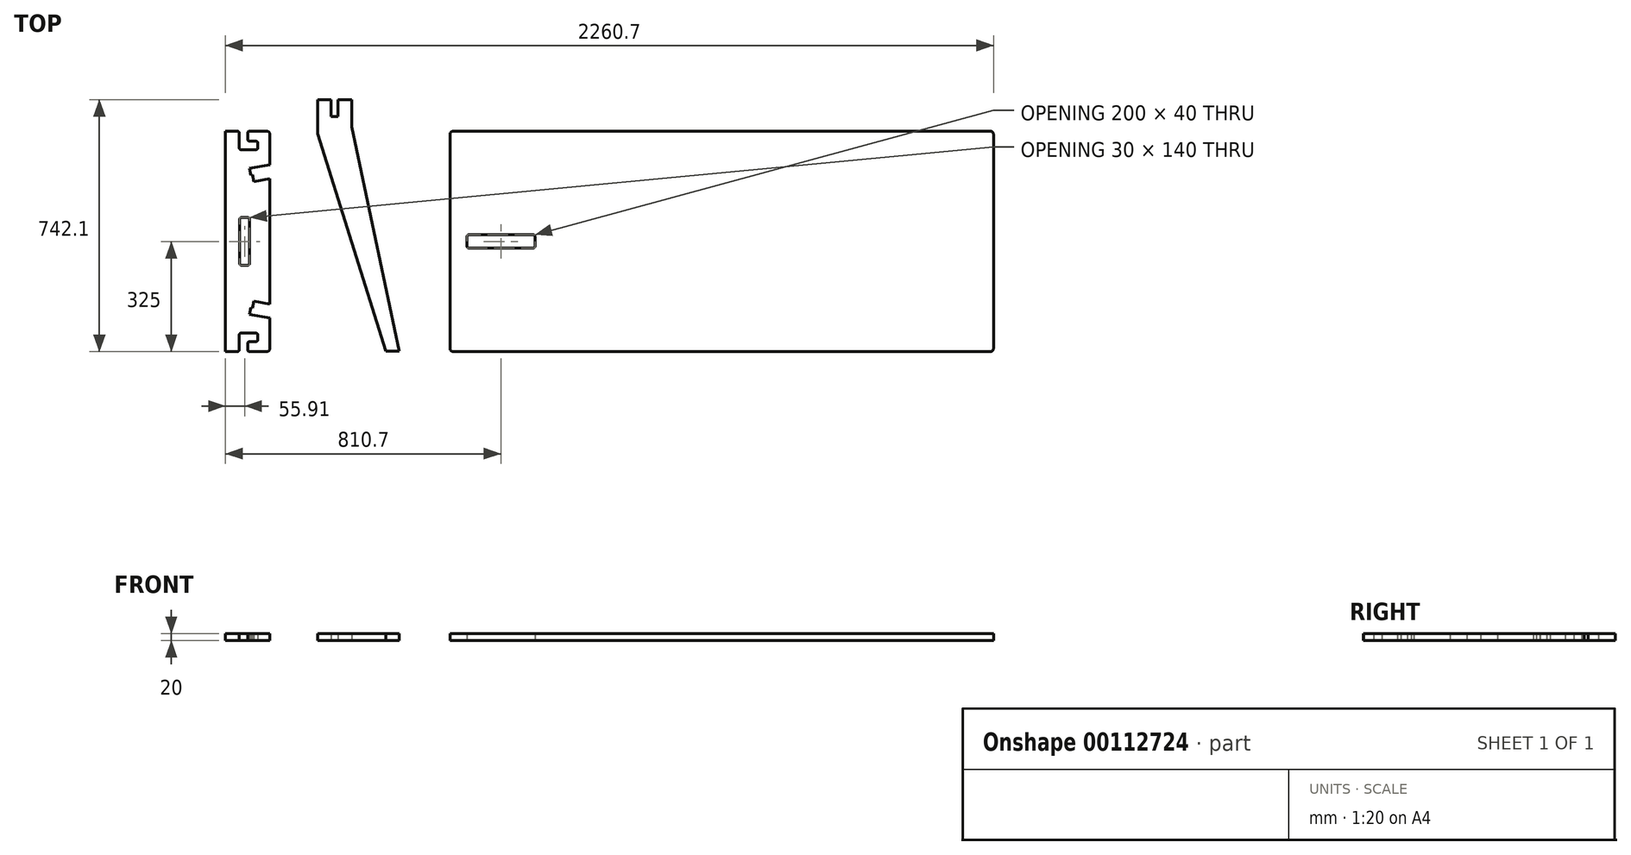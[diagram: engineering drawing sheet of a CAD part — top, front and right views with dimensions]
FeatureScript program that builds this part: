
annotation { "Feature Type Name" : "Feature", "Feature Type Description" : "" }
export const myFeature = defineFeature(function(context is Context, id is Id, definition is map)
    precondition{}
    {
        {
            assignVariable(context, id + "F0", {"name" : "stock_thickness", "anyValue" : 20});
        }
        {
            var Q0;
            Q0=qCreatedBy(makeId("Top.planeOp"),FACE);
            var sketch = newSketch(context, id + "F1", { "sketchPlane" : qUnion([Q0])});
            skLineSegment(sketch, "E0.bottom", {"start": v(10, 0) * mm, "end": v(1590, 0) * mm});
            skLineSegment(sketch, "E0.top", {"start": v(10, 650) * mm, "end": v(1590, 650) * mm});
            skLineSegment(sketch, "E0.left", {"start": v(0, 10) * mm, "end": v(0, 640) * mm});
            skLineSegment(sketch, "E0.right", {"start": v(1600, 10) * mm, "end": v(1600, 640) * mm});
            skPoint(sketch, "E1.visualSharp", {"position": v(0, 650) * mm});
            skArc(sketch, "E1.filletArc", {"start": v(10, 650) * mm, "mid": v(2.93, 647.07) * mm, "end": v(0, 640) * mm});
            skPoint(sketch, "E2.visualSharp", {"position": v(1600, 650) * mm});
            skArc(sketch, "E2.filletArc", {"start": v(1600, 640) * mm, "mid": v(1597.07, 647.07) * mm, "end": v(1590, 650) * mm});
            skPoint(sketch, "E3.visualSharp", {"position": v(1600, 0) * mm});
            skArc(sketch, "E3.filletArc", {"start": v(1590, 0) * mm, "mid": v(1597.07, 2.93) * mm, "end": v(1600, 10) * mm});
            skPoint(sketch, "E4.visualSharp", {"position": v(0, 0) * mm});
            skArc(sketch, "E4.filletArc", {"start": v(0, 10) * mm, "mid": v(2.93, 2.93) * mm, "end": v(10, 0) * mm});
            skLineSegment(sketch, "E5", {"start": v(0, 325) * mm, "end": v(1600, 325) * mm, "construction": true});
            skLineSegment(sketch, "E6", {"start": v(800, 650) * mm, "end": v(800, 0) * mm, "construction": true});
            skCircle(sketch, "E7", {"center": v(800, 325) * mm, "radius": 30 * mm, "construction": true});
            skLineSegment(sketch, "E8.bottom", {"start": v(1544, 305) * mm, "end": v(1356, 305) * mm});
            skLineSegment(sketch, "E8.top", {"start": v(1544, 345) * mm, "end": v(1356, 345) * mm});
            skLineSegment(sketch, "E8.left", {"start": v(1550, 311) * mm, "end": v(1550, 339) * mm});
            skLineSegment(sketch, "E8.right", {"start": v(1350, 311) * mm, "end": v(1350, 339) * mm});
            skPoint(sketch, "E8.middle", {"position": v(1450, 325) * mm});
            skLineSegment(sketch, "E9.bottom", {"start": v(1544, 355) * mm, "end": v(1356, 355) * mm});
            skLineSegment(sketch, "E9.top", {"start": v(1544, 369) * mm, "end": v(1356, 369) * mm});
            skLineSegment(sketch, "E9.left", {"start": v(1550, 361) * mm, "end": v(1550, 363) * mm});
            skLineSegment(sketch, "E9.right", {"start": v(1350, 361) * mm, "end": v(1350, 363) * mm});
            skPoint(sketch, "E9.middle", {"position": v(1450, 362) * mm});
            skCircle(sketch, "E10.1.0.0", {"center": v(885, 325) * mm, "radius": 30 * mm, "construction": true});
            skCircle(sketch, "E10.2.0.0", {"center": v(970, 325) * mm, "radius": 30 * mm, "construction": true});
            skLineSegment(sketch, "E10.direction1", {"start": v(800, 325) * mm, "end": v(885, 325) * mm, "construction": true});
            skCircle(sketch, "E11.0.3.0", {"center": v(1055, 325) * mm, "radius": 30 * mm, "construction": true});
            skPoint(sketch, "E12.visualSharp", {"position": v(1350, 345) * mm});
            skArc(sketch, "E12.filletArc", {"start": v(1356, 345) * mm, "mid": v(1351.76, 343.24) * mm, "end": v(1350, 339) * mm});
            skPoint(sketch, "E13.visualSharp", {"position": v(1550, 345) * mm});
            skArc(sketch, "E13.filletArc", {"start": v(1550, 339) * mm, "mid": v(1548.24, 343.24) * mm, "end": v(1544, 345) * mm});
            skPoint(sketch, "E14.visualSharp", {"position": v(1550, 305) * mm});
            skArc(sketch, "E14.filletArc", {"start": v(1544, 305) * mm, "mid": v(1548.24, 306.76) * mm, "end": v(1550, 311) * mm});
            skPoint(sketch, "E15.visualSharp", {"position": v(1350, 305) * mm});
            skArc(sketch, "E15.filletArc", {"start": v(1350, 311) * mm, "mid": v(1351.76, 306.76) * mm, "end": v(1356, 305) * mm});
            skPoint(sketch, "E16.visualSharp", {"position": v(1350, 369) * mm});
            skArc(sketch, "E16.filletArc", {"start": v(1356, 369) * mm, "mid": v(1351.76, 367.24) * mm, "end": v(1350, 363) * mm});
            skPoint(sketch, "E17.visualSharp", {"position": v(1350, 355) * mm});
            skArc(sketch, "E17.filletArc", {"start": v(1350, 361) * mm, "mid": v(1351.76, 356.76) * mm, "end": v(1356, 355) * mm});
            skPoint(sketch, "E18.visualSharp", {"position": v(1550, 355) * mm});
            skArc(sketch, "E18.filletArc", {"start": v(1544, 355) * mm, "mid": v(1548.24, 356.76) * mm, "end": v(1550, 361) * mm});
            skPoint(sketch, "E19.visualSharp", {"position": v(1550, 369) * mm});
            skArc(sketch, "E19.filletArc", {"start": v(1550, 363) * mm, "mid": v(1548.24, 367.24) * mm, "end": v(1544, 369) * mm});
            skArc(sketch, "E20.MirrorCS", {"start": v(250, 361) * mm, "mid": v(248.24, 356.76) * mm, "end": v(244, 355) * mm});
            skArc(sketch, "E21.MirrorCS", {"start": v(244, 369) * mm, "mid": v(248.24, 367.24) * mm, "end": v(250, 363) * mm});
            skArc(sketch, "E22.MirrorCS", {"start": v(50, 363) * mm, "mid": v(51.76, 367.24) * mm, "end": v(56, 369) * mm});
            skArc(sketch, "E23.MirrorCS", {"start": v(56, 355) * mm, "mid": v(51.76, 356.76) * mm, "end": v(50, 361) * mm});
            skArc(sketch, "E24.MirrorCS", {"start": v(50, 339) * mm, "mid": v(51.76, 343.24) * mm, "end": v(56, 345) * mm});
            skArc(sketch, "E25.MirrorCS", {"start": v(250, 311) * mm, "mid": v(248.24, 306.76) * mm, "end": v(244, 305) * mm});
            skArc(sketch, "E26.MirrorCS", {"start": v(244, 345) * mm, "mid": v(248.24, 343.24) * mm, "end": v(250, 339) * mm});
            skArc(sketch, "E27.MirrorCS", {"start": v(56, 305) * mm, "mid": v(51.76, 306.76) * mm, "end": v(50, 311) * mm});
            skPoint(sketch, "E28.MirrorP", {"position": v(250, 355) * mm});
            skPoint(sketch, "E29.MirrorP", {"position": v(50, 355) * mm});
            skCircle(sketch, "E30.MirrorC", {"center": v(630, 325) * mm, "radius": 30 * mm, "construction": true});
            skPoint(sketch, "E31.MirrorP", {"position": v(50, 369) * mm});
            skLineSegment(sketch, "E32.MirrorCS", {"start": v(50, 311) * mm, "end": v(50, 339) * mm});
            skLineSegment(sketch, "E33.MirrorCS", {"start": v(250, 311) * mm, "end": v(250, 339) * mm});
            skLineSegment(sketch, "E34.MirrorCS", {"start": v(56, 355) * mm, "end": v(244, 355) * mm});
            skPoint(sketch, "E35.MirrorP", {"position": v(50, 305) * mm});
            skCircle(sketch, "E36.MirrorC", {"center": v(715, 325) * mm, "radius": 30 * mm, "construction": true});
            skPoint(sketch, "E37.MirrorP", {"position": v(150, 362) * mm});
            skLineSegment(sketch, "E38.MirrorCS", {"start": v(56, 369) * mm, "end": v(244, 369) * mm});
            skPoint(sketch, "E39.MirrorP", {"position": v(50, 345) * mm});
            skPoint(sketch, "E40.MirrorP", {"position": v(150, 325) * mm});
            skCircle(sketch, "E41.MirrorC", {"center": v(545, 325) * mm, "radius": 30 * mm, "construction": true});
            skPoint(sketch, "E42.MirrorP", {"position": v(250, 369) * mm});
            skLineSegment(sketch, "E43.MirrorCS", {"start": v(56, 305) * mm, "end": v(244, 305) * mm});
            skLineSegment(sketch, "E44.MirrorCS", {"start": v(56, 345) * mm, "end": v(244, 345) * mm});
            skPoint(sketch, "E45.MirrorP", {"position": v(250, 345) * mm});
            skPoint(sketch, "E46.MirrorP", {"position": v(250, 305) * mm});
            skArc(sketch, "E47.MirrorCS", {"start": v(50, 287) * mm, "mid": v(51.76, 282.76) * mm, "end": v(56, 281) * mm});
            skArc(sketch, "E48.MirrorCS", {"start": v(244, 281) * mm, "mid": v(248.24, 282.76) * mm, "end": v(250, 287) * mm});
            skLineSegment(sketch, "E49.MirrorCS", {"start": v(56, 295) * mm, "end": v(244, 295) * mm});
            skPoint(sketch, "E50.MirrorP", {"position": v(250, 281) * mm});
            skLineSegment(sketch, "E51.MirrorCS", {"start": v(56, 281) * mm, "end": v(244, 281) * mm});
            skArc(sketch, "E52.MirrorCS", {"start": v(56, 295) * mm, "mid": v(51.76, 293.24) * mm, "end": v(50, 289) * mm});
            skArc(sketch, "E53.MirrorCS", {"start": v(250, 289) * mm, "mid": v(248.24, 293.24) * mm, "end": v(244, 295) * mm});
            skPoint(sketch, "E54.MirrorP", {"position": v(150, 288) * mm});
            skPoint(sketch, "E55.MirrorP", {"position": v(50, 281) * mm});
            skArc(sketch, "E56.MirrorCS", {"start": v(1350, 289) * mm, "mid": v(1351.76, 293.24) * mm, "end": v(1356, 295) * mm});
            skArc(sketch, "E57.MirrorCS", {"start": v(1550, 287) * mm, "mid": v(1548.24, 282.76) * mm, "end": v(1544, 281) * mm});
            skArc(sketch, "E58.MirrorCS", {"start": v(1544, 295) * mm, "mid": v(1548.24, 293.24) * mm, "end": v(1550, 289) * mm});
            skArc(sketch, "E59.MirrorCS", {"start": v(1356, 281) * mm, "mid": v(1351.76, 282.76) * mm, "end": v(1350, 287) * mm});
            skPoint(sketch, "E60.MirrorP", {"position": v(1350, 295) * mm});
            skPoint(sketch, "E61.MirrorP", {"position": v(1550, 295) * mm});
            skPoint(sketch, "E62.MirrorP", {"position": v(1450, 288) * mm});
            skPoint(sketch, "E63.MirrorP", {"position": v(1350, 281) * mm});
            skLineSegment(sketch, "E64.MirrorCS", {"start": v(1544, 295) * mm, "end": v(1356, 295) * mm});
            skLineSegment(sketch, "E65.MirrorCS", {"start": v(1544, 281) * mm, "end": v(1356, 281) * mm});
            skPoint(sketch, "E66.MirrorP", {"position": v(1550, 281) * mm});
            skSolve(sketch);
        }
        {
            var Q0;
            Q0=qCreatedBy(makeId("Top.planeOp"),FACE);
            var sketch = newSketch(context, id + "F2", { "sketchPlane" : qUnion([Q0])});
            skLineSegment(sketch, "E67.bottom", {"start": v(-148.98, 2.1) * mm, "end": v(-188.98, 2.1) * mm});
            skLineSegment(sketch, "E67.top", {"start": v(-288.98, 742.1) * mm, "end": v(-329.98, 742.1) * mm});
            skLineSegment(sketch, "E68", {"start": v(-288.98, 742.1) * mm, "end": v(-288.98, 662.1) * mm});
            skLineSegment(sketch, "E69", {"start": v(-288.98, 662.1) * mm, "end": v(-148.98, 2.1) * mm});
            skLineSegment(sketch, "E70", {"start": v(-388.98, 642.1) * mm, "end": v(-188.98, 2.1) * mm});
            skLineSegment(sketch, "E71", {"start": v(-388.98, 742.1) * mm, "end": v(-388.98, 2.1) * mm, "construction": true});
            skLineSegment(sketch, "E72", {"start": v(-388.98, 742.1) * mm, "end": v(-388.98, 642.1) * mm});
            skLineSegment(sketch, "E73.bottom", {"start": v(-329.98, 692.1) * mm, "end": v(-349.98, 692.1) * mm});
            skLineSegment(sketch, "E73.left", {"start": v(-329.98, 692.1) * mm, "end": v(-329.98, 742.1) * mm});
            skLineSegment(sketch, "E73.right", {"start": v(-349.98, 692.1) * mm, "end": v(-349.98, 742.1) * mm});
            skPoint(sketch, "E73.middle", {"position": v(-338.98, 742.1) * mm});
            skLineSegment(sketch, "E74.trimOffspring", {"start": v(-349.98, 742.1) * mm, "end": v(-388.98, 742.1) * mm});
            skSolve(sketch);
        }
        {
            var Q0;
            Q0=qCreatedBy(makeId("Top.planeOp"),FACE);
            var sketch = newSketch(context, id + "F3", { "sketchPlane" : qUnion([Q0])});
            skLineSegment(sketch, "E75.bottom", {"start": v(-540.7, 0) * mm, "end": v(-589.7, 0) * mm});
            skLineSegment(sketch, "E75.top", {"start": v(-540.7, 650) * mm, "end": v(-589.7, 650) * mm});
            skLineSegment(sketch, "E75.left", {"start": v(-530.7, 10) * mm, "end": v(-530.7, 640) * mm});
            skLineSegment(sketch, "E75.right", {"start": v(-660.7, 0) * mm, "end": v(-660.7, 650) * mm});
            skLineSegment(sketch, "E76", {"start": v(-530.7, 325) * mm, "end": v(-589.8, 325) * mm, "construction": true});
            skLineSegment(sketch, "E77", {"start": v(-530.7, 100) * mm, "end": v(-589.8, 110.32) * mm});
            skLineSegment(sketch, "E78", {"start": v(-589.8, 110.32) * mm, "end": v(-586.37, 130.02) * mm});
            skLineSegment(sketch, "E79", {"start": v(-586.37, 130.02) * mm, "end": v(-581.44, 129.16) * mm});
            skLineSegment(sketch, "E80", {"start": v(-581.44, 129.16) * mm, "end": v(-578, 148.86) * mm});
            skLineSegment(sketch, "E81", {"start": v(-578, 148.86) * mm, "end": v(-530.7, 140.6) * mm});
            skLineSegment(sketch, "E82", {"start": v(-595.7, 6) * mm, "end": v(-595.7, 24) * mm});
            skLineSegment(sketch, "E83", {"start": v(-589.7, 30) * mm, "end": v(-571.7, 30) * mm});
            skLineSegment(sketch, "E84", {"start": v(-620.7, 6) * mm, "end": v(-620.7, 49) * mm});
            skLineSegment(sketch, "E85", {"start": v(-614.7, 55) * mm, "end": v(-571.7, 55) * mm});
            skLineSegment(sketch, "E86", {"start": v(-565.7, 49) * mm, "end": v(-565.7, 36) * mm});
            skLineSegment(sketch, "E87.trimOffspring", {"start": v(-626.7, 0) * mm, "end": v(-660.7, 0) * mm});
            skPoint(sketch, "E88.visualSharp", {"position": v(-595.7, 30) * mm});
            skArc(sketch, "E88.filletArc", {"start": v(-589.7, 30) * mm, "mid": v(-593.94, 28.24) * mm, "end": v(-595.7, 24) * mm});
            skPoint(sketch, "E89.visualSharp", {"position": v(-620.7, 0) * mm});
            skArc(sketch, "E89.filletArc", {"start": v(-626.7, 0) * mm, "mid": v(-622.46, 1.76) * mm, "end": v(-620.7, 6) * mm});
            skPoint(sketch, "E90.visualSharp", {"position": v(-595.7, 0) * mm});
            skArc(sketch, "E90.filletArc", {"start": v(-595.7, 6) * mm, "mid": v(-593.94, 1.76) * mm, "end": v(-589.7, 0) * mm});
            skPoint(sketch, "E91.visualSharp", {"position": v(-565.7, 30) * mm});
            skArc(sketch, "E91.filletArc", {"start": v(-571.7, 30) * mm, "mid": v(-567.46, 31.76) * mm, "end": v(-565.7, 36) * mm});
            skPoint(sketch, "E92.visualSharp", {"position": v(-565.7, 55) * mm});
            skArc(sketch, "E92.filletArc", {"start": v(-565.7, 49) * mm, "mid": v(-567.46, 53.24) * mm, "end": v(-571.7, 55) * mm});
            skPoint(sketch, "E93.visualSharp", {"position": v(-620.7, 55) * mm});
            skArc(sketch, "E93.filletArc", {"start": v(-614.7, 55) * mm, "mid": v(-618.94, 53.24) * mm, "end": v(-620.7, 49) * mm});
            skLineSegment(sketch, "E94.top", {"start": v(-613.8, 255) * mm, "end": v(-595.8, 255) * mm});
            skLineSegment(sketch, "E94.left", {"start": v(-619.8, 325) * mm, "end": v(-619.8, 261) * mm});
            skLineSegment(sketch, "E94.right", {"start": v(-589.8, 325) * mm, "end": v(-589.8, 261) * mm});
            skLineSegment(sketch, "E95.trimOffspring", {"start": v(-619.8, 325) * mm, "end": v(-660.7, 325) * mm, "construction": true});
            skLineSegment(sketch, "E96", {"start": v(-619.8, 325) * mm, "end": v(-589.8, 325) * mm, "construction": true});
            skArc(sketch, "E97.MirrorCS", {"start": v(-626.7, 650) * mm, "mid": v(-622.46, 648.24) * mm, "end": v(-620.7, 644) * mm});
            skArc(sketch, "E98.MirrorCS", {"start": v(-595.7, 644) * mm, "mid": v(-593.94, 648.24) * mm, "end": v(-589.7, 650) * mm});
            skLineSegment(sketch, "E99.MirrorCS", {"start": v(-595.7, 644) * mm, "end": v(-595.7, 626) * mm});
            skArc(sketch, "E100.MirrorCS", {"start": v(-589.7, 620) * mm, "mid": v(-593.94, 621.76) * mm, "end": v(-595.7, 626) * mm});
            skLineSegment(sketch, "E101.MirrorCS", {"start": v(-589.7, 620) * mm, "end": v(-571.7, 620) * mm});
            skArc(sketch, "E102.MirrorCS", {"start": v(-571.7, 620) * mm, "mid": v(-567.46, 618.24) * mm, "end": v(-565.7, 614) * mm});
            skLineSegment(sketch, "E103.MirrorCS", {"start": v(-565.7, 601) * mm, "end": v(-565.7, 614) * mm});
            skArc(sketch, "E104.MirrorCS", {"start": v(-565.7, 601) * mm, "mid": v(-567.46, 596.76) * mm, "end": v(-571.7, 595) * mm});
            skLineSegment(sketch, "E105.MirrorCS", {"start": v(-614.7, 595) * mm, "end": v(-571.7, 595) * mm});
            skArc(sketch, "E106.MirrorCS", {"start": v(-614.7, 595) * mm, "mid": v(-618.94, 596.76) * mm, "end": v(-620.7, 601) * mm});
            skLineSegment(sketch, "E107.MirrorCS", {"start": v(-620.7, 644) * mm, "end": v(-620.7, 601) * mm});
            skLineSegment(sketch, "E108.MirrorCS", {"start": v(-613.8, 395) * mm, "end": v(-595.8, 395) * mm});
            skLineSegment(sketch, "E109.MirrorCS", {"start": v(-589.8, 325) * mm, "end": v(-589.8, 389) * mm});
            skLineSegment(sketch, "E110.MirrorCS", {"start": v(-619.8, 325) * mm, "end": v(-619.8, 389) * mm});
            skLineSegment(sketch, "E111.trimOffspring", {"start": v(-626.7, 650) * mm, "end": v(-660.7, 650) * mm});
            skPoint(sketch, "E112.visualSharp", {"position": v(-530.7, 0) * mm});
            skArc(sketch, "E112.filletArc", {"start": v(-540.7, 0) * mm, "mid": v(-533.63, 2.93) * mm, "end": v(-530.7, 10) * mm});
            skPoint(sketch, "E113.visualSharp", {"position": v(-530.7, 650) * mm});
            skArc(sketch, "E113.filletArc", {"start": v(-530.7, 640) * mm, "mid": v(-533.63, 647.07) * mm, "end": v(-540.7, 650) * mm});
            skLineSegment(sketch, "E114.MirrorCS", {"start": v(-578, 501.14) * mm, "end": v(-530.7, 509.4) * mm});
            skLineSegment(sketch, "E115.MirrorCS", {"start": v(-581.44, 520.84) * mm, "end": v(-578, 501.14) * mm});
            skLineSegment(sketch, "E116.MirrorCS", {"start": v(-586.37, 519.98) * mm, "end": v(-581.44, 520.84) * mm});
            skLineSegment(sketch, "E117.MirrorCS", {"start": v(-530.7, 550) * mm, "end": v(-589.8, 539.68) * mm});
            skLineSegment(sketch, "E118.MirrorCS", {"start": v(-589.8, 539.68) * mm, "end": v(-586.37, 519.98) * mm});
            skPoint(sketch, "E119.visualSharp", {"position": v(-619.8, 395) * mm});
            skArc(sketch, "E119.filletArc", {"start": v(-613.8, 395) * mm, "mid": v(-618.03, 393.24) * mm, "end": v(-619.8, 389) * mm});
            skPoint(sketch, "E120.visualSharp", {"position": v(-619.8, 255) * mm});
            skArc(sketch, "E120.filletArc", {"start": v(-619.8, 261) * mm, "mid": v(-618.03, 256.76) * mm, "end": v(-613.8, 255) * mm});
            skPoint(sketch, "E121.visualSharp", {"position": v(-589.8, 255) * mm});
            skArc(sketch, "E121.filletArc", {"start": v(-595.8, 255) * mm, "mid": v(-591.55, 256.76) * mm, "end": v(-589.8, 261) * mm});
            skPoint(sketch, "E122.visualSharp", {"position": v(-589.8, 395) * mm});
            skArc(sketch, "E122.filletArc", {"start": v(-589.8, 389) * mm, "mid": v(-591.55, 393.24) * mm, "end": v(-595.8, 395) * mm});
            skSolve(sketch);
        }
        {
            var Q0;
            Q0=makeQuery(id+"F3.imprint","IMPRINT",FACE,{"disambiguationData":[TD([[makeQuery(id+"F3.imprint","IMPRINT",EDGE,{"derivedFrom":sQuery(id+"F3.wireOp",EDGE,"E75.bottom")}),-1.0]])]});
            extrude(context, id + "F4", {"entities" : qUnion([Q0]), "depth" : (getVariable(context, 'stock_thickness')) * mm});
        }
        {
            var Q0;
            Q0 = qSketchRegion(id + "F2", true);
            var Q1;
            Q1=makeQuery(id+"F2.imprint","IMPRINT",FACE,{"disambiguationData":[TD([[makeQuery(id+"F2.imprint","IMPRINT",EDGE,{"derivedFrom":sQuery(id+"F2.wireOp",EDGE,"E67.bottom")}),-1.0]])]});
            extrude(context, id + "F5", {"entities" : qUnion([Q0, Q1]), "depth" : (getVariable(context, 'stock_thickness')) * mm});
        }
        {
            var Q0;
            Q0=makeQuery(id+"F1.imprint","IMPRINT",FACE,{"disambiguationData":[TD([[makeQuery(id+"F1.imprint","IMPRINT",EDGE,{"derivedFrom":sQuery(id+"F1.wireOp",EDGE,"E0.bottom")}),1.0]])]});
            var Q1;
            Q1=makeQuery(id+"F1.imprint","IMPRINT",FACE,{"disambiguationData":[TD([[makeQuery(id+"F1.imprint","IMPRINT",EDGE,{"derivedFrom":sQuery(id+"F1.wireOp",EDGE,"E9.bottom")}),-1.0]])]});
            var Q2;
            Q2=makeQuery(id+"F1.imprint","IMPRINT",FACE,{"disambiguationData":[TD([[makeQuery(id+"F1.imprint","IMPRINT",EDGE,{"derivedFrom":sQuery(id+"F1.wireOp",EDGE,"E24.MirrorCS")}),-1.0]])]});
            var Q3;
            Q3=makeQuery(id+"F1.imprint","IMPRINT",FACE,{"disambiguationData":[TD([[makeQuery(id+"F1.imprint","IMPRINT",EDGE,{"derivedFrom":sQuery(id+"F1.wireOp",EDGE,"E8.bottom")}),-1.0]])]});
            extrude(context, id + "F6", {"entities" : qUnion([Q0, Q1, Q2, Q3]), "depth" : (getVariable(context, 'stock_thickness')) * mm});
        }
    });
